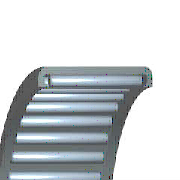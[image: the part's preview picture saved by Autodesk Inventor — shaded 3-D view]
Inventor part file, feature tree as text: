
AUTODESK INVENTOR PART (.ipt)
format: ipt  version: 2025.2 (Build 292293000, 293)  size: 270,848 bytes
history: native  units: mm (DEFAULTED — no unit token found)
features: other x2, pattern_circular x1
ambient origin geometry x8: Origin, YZ Plane, XZ Plane, XY Plane, X Axis, Y Axis, Z Axis, Center Point
bodies: Solid1 (feature_tree)
feature tree (3):
  other  "Körper"
  other  "Rolle"
  pattern_circular  "Rollen"  Angle=90.0deg  [1 undecoded]
note: 1 required parameter value undecoded (feature->parameter linkage not recoverable at this tier; creation-order binding heuristic only, values carry confidence <= 0.55)
